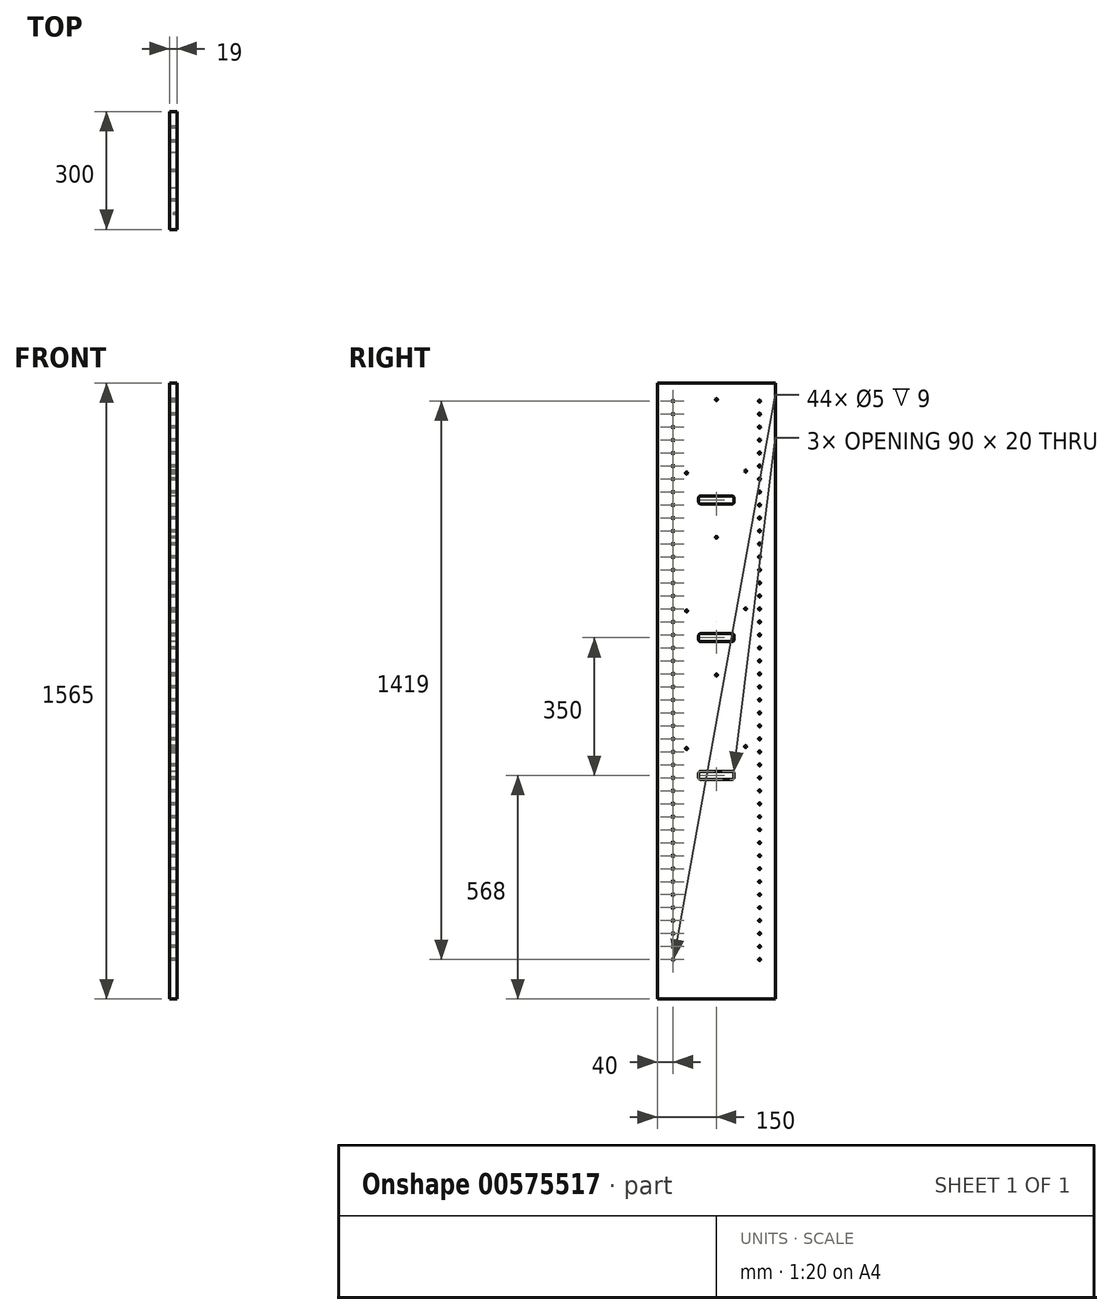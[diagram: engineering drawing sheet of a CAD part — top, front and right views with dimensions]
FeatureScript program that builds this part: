
annotation { "Feature Type Name" : "Feature", "Feature Type Description" : "" }
export const myFeature = defineFeature(function(context is Context, id is Id, definition is map)
    precondition{}
    {
        {
            var Q0;
            Q0=qCreatedBy(makeId("Front.planeOp"),FACE);
            var sketch = newSketch(context, id + "F0", { "sketchPlane" : qUnion([Q0])});
            skLineSegment(sketch, "E0.bottom", {"start": v(0, 0) * mm, "end": v(1000, 0) * mm, "construction": true});
            skLineSegment(sketch, "E0.left", {"start": v(0, 0) * mm, "end": v(0, 1590) * mm, "construction": true});
            skLineSegment(sketch, "E0.right", {"start": v(1000, 0) * mm, "end": v(1000, 1590) * mm, "construction": true});
            skLineSegment(sketch, "E1", {"start": v(500, 1590) * mm, "end": v(500, 0) * mm, "construction": true});
            skLineSegment(sketch, "E2.bottom", {"start": v(0, 1590) * mm, "end": v(1000, 1590) * mm, "construction": true});
            skLineSegment(sketch, "E2.left", {"start": v(0, 1590) * mm, "end": v(0, 290) * mm, "construction": true});
            skSolve(sketch);
        }
        {
            var Q0;
            Q0=qCreatedBy(makeId("Right.planeOp"),FACE);
            var sketch = newSketch(context, id + "F1", { "sketchPlane" : qUnion([Q0])});
            skLineSegment(sketch, "E3.bottom", {"start": v(0, 1590) * mm, "end": v(300, 1590) * mm});
            skLineSegment(sketch, "E3.top", {"start": v(0, 25) * mm, "end": v(300, 25) * mm});
            skLineSegment(sketch, "E3.left", {"start": v(0, 1590) * mm, "end": v(0, 25) * mm});
            skLineSegment(sketch, "E3.right", {"start": v(300, 1590) * mm, "end": v(300, 25) * mm});
            skCircle(sketch, "E4", {"center": v(150, 1548) * mm, "radius": 2.5 * mm});
            skCircle(sketch, "E5", {"center": v(74.47, 1361.2) * mm, "radius": 2.5 * mm});
            skCircle(sketch, "E6.MirrorC", {"center": v(224.47, 1366.34) * mm, "radius": 2.5 * mm});
            skLineSegment(sketch, "E7.bottom", {"start": v(190, 1283) * mm, "end": v(110, 1283) * mm});
            skLineSegment(sketch, "E7.top", {"start": v(190, 1303) * mm, "end": v(110, 1303) * mm});
            skLineSegment(sketch, "E7.left", {"start": v(195, 1288) * mm, "end": v(195, 1298) * mm});
            skLineSegment(sketch, "E7.right", {"start": v(105, 1288) * mm, "end": v(105, 1298) * mm});
            skPoint(sketch, "E7.middle", {"position": v(150, 1293) * mm});
            skPoint(sketch, "E8.visualSharp", {"position": v(105, 1303) * mm});
            skArc(sketch, "E8.filletArc", {"start": v(110, 1303) * mm, "mid": v(106.46, 1301.54) * mm, "end": v(105, 1298) * mm});
            skPoint(sketch, "E9.visualSharp", {"position": v(105, 1283) * mm});
            skArc(sketch, "E9.filletArc", {"start": v(105, 1288) * mm, "mid": v(106.46, 1284.46) * mm, "end": v(110, 1283) * mm});
            skPoint(sketch, "E10.visualSharp", {"position": v(195, 1283) * mm});
            skArc(sketch, "E10.filletArc", {"start": v(190, 1283) * mm, "mid": v(193.54, 1284.46) * mm, "end": v(195, 1288) * mm});
            skPoint(sketch, "E11.visualSharp", {"position": v(195, 1303) * mm});
            skArc(sketch, "E11.filletArc", {"start": v(195, 1298) * mm, "mid": v(193.54, 1301.54) * mm, "end": v(190, 1303) * mm});
            skLineSegment(sketch, "E12", {"start": v(150, 1590) * mm, "end": v(150, 25) * mm, "construction": true});
            skLineSegment(sketch, "E13.0.1.0", {"start": v(190, 933) * mm, "end": v(110, 933) * mm});
            skLineSegment(sketch, "E13.0.1.1", {"start": v(190, 953) * mm, "end": v(110, 953) * mm});
            skPoint(sketch, "E13.0.1.2", {"position": v(195, 933) * mm});
            skPoint(sketch, "E13.0.1.3", {"position": v(150, 943) * mm});
            skPoint(sketch, "E13.0.1.4", {"position": v(195, 953) * mm});
            skPoint(sketch, "E13.0.1.5", {"position": v(105, 933) * mm});
            skCircle(sketch, "E13.0.1.6", {"center": v(150, 1198) * mm, "radius": 2.5 * mm});
            skCircle(sketch, "E13.0.1.7", {"center": v(74.47, 1011.2) * mm, "radius": 2.5 * mm});
            skPoint(sketch, "E13.0.1.8", {"position": v(105, 953) * mm});
            skCircle(sketch, "E13.0.1.9", {"center": v(224.47, 1016.34) * mm, "radius": 2.5 * mm});
            skArc(sketch, "E13.0.1.10", {"start": v(110, 953) * mm, "mid": v(106.46, 951.54) * mm, "end": v(105, 948) * mm});
            skLineSegment(sketch, "E13.0.1.11", {"start": v(105, 938) * mm, "end": v(105, 948) * mm});
            skLineSegment(sketch, "E13.0.1.12", {"start": v(195, 938) * mm, "end": v(195, 948) * mm});
            skArc(sketch, "E13.0.1.13", {"start": v(105, 938) * mm, "mid": v(106.46, 934.46) * mm, "end": v(110, 933) * mm});
            skArc(sketch, "E13.0.1.14", {"start": v(195, 948) * mm, "mid": v(193.54, 951.54) * mm, "end": v(190, 953) * mm});
            skArc(sketch, "E13.0.1.15", {"start": v(190, 933) * mm, "mid": v(193.54, 934.46) * mm, "end": v(195, 938) * mm});
            skLineSegment(sketch, "E13.0.2.0", {"start": v(190, 583) * mm, "end": v(110, 583) * mm});
            skLineSegment(sketch, "E13.0.2.1", {"start": v(190, 603) * mm, "end": v(110, 603) * mm});
            skPoint(sketch, "E13.0.2.2", {"position": v(195, 583) * mm});
            skPoint(sketch, "E13.0.2.3", {"position": v(150, 593) * mm});
            skPoint(sketch, "E13.0.2.4", {"position": v(195, 603) * mm});
            skPoint(sketch, "E13.0.2.5", {"position": v(105, 583) * mm});
            skCircle(sketch, "E13.0.2.6", {"center": v(150, 848) * mm, "radius": 2.5 * mm});
            skCircle(sketch, "E13.0.2.7", {"center": v(74.47, 661.2) * mm, "radius": 2.5 * mm});
            skPoint(sketch, "E13.0.2.8", {"position": v(105, 603) * mm});
            skCircle(sketch, "E13.0.2.9", {"center": v(224.47, 666.34) * mm, "radius": 2.5 * mm});
            skArc(sketch, "E13.0.2.10", {"start": v(110, 603) * mm, "mid": v(106.46, 601.54) * mm, "end": v(105, 598) * mm});
            skLineSegment(sketch, "E13.0.2.11", {"start": v(105, 588) * mm, "end": v(105, 598) * mm});
            skLineSegment(sketch, "E13.0.2.12", {"start": v(195, 588) * mm, "end": v(195, 598) * mm});
            skArc(sketch, "E13.0.2.13", {"start": v(105, 588) * mm, "mid": v(106.46, 584.46) * mm, "end": v(110, 583) * mm});
            skArc(sketch, "E13.0.2.14", {"start": v(195, 598) * mm, "mid": v(193.54, 601.54) * mm, "end": v(190, 603) * mm});
            skArc(sketch, "E13.0.2.15", {"start": v(190, 583) * mm, "mid": v(193.54, 584.46) * mm, "end": v(195, 588) * mm});
            skLineSegment(sketch, "E13.direction1", {"start": v(105, 1283) * mm, "end": v(130, 1283) * mm, "construction": true});
            skLineSegment(sketch, "E13.direction2", {"start": v(105, 1283) * mm, "end": v(105, 933) * mm, "construction": true});
            skCircle(sketch, "E14", {"center": v(40, 125) * mm, "radius": 2.5 * mm});
            skCircle(sketch, "E15.0.1.0", {"center": v(40, 158) * mm, "radius": 2.5 * mm});
            skCircle(sketch, "E15.0.2.0", {"center": v(40, 191) * mm, "radius": 2.5 * mm});
            skCircle(sketch, "E15.0.3.0", {"center": v(40, 224) * mm, "radius": 2.5 * mm});
            skCircle(sketch, "E15.0.4.0", {"center": v(40, 257) * mm, "radius": 2.5 * mm});
            skCircle(sketch, "E15.0.5.0", {"center": v(40, 290) * mm, "radius": 2.5 * mm});
            skCircle(sketch, "E15.0.6.0", {"center": v(40, 323) * mm, "radius": 2.5 * mm});
            skCircle(sketch, "E15.0.7.0", {"center": v(40, 356) * mm, "radius": 2.5 * mm});
            skCircle(sketch, "E15.0.8.0", {"center": v(40, 389) * mm, "radius": 2.5 * mm});
            skCircle(sketch, "E15.0.9.0", {"center": v(40, 422) * mm, "radius": 2.5 * mm});
            skCircle(sketch, "E15.0.10.0", {"center": v(40, 455) * mm, "radius": 2.5 * mm});
            skCircle(sketch, "E15.0.11.0", {"center": v(40, 488) * mm, "radius": 2.5 * mm});
            skCircle(sketch, "E15.0.12.0", {"center": v(40, 521) * mm, "radius": 2.5 * mm});
            skCircle(sketch, "E15.0.13.0", {"center": v(40, 554) * mm, "radius": 2.5 * mm});
            skCircle(sketch, "E15.0.14.0", {"center": v(40, 587) * mm, "radius": 2.5 * mm});
            skCircle(sketch, "E15.0.15.0", {"center": v(40, 620) * mm, "radius": 2.5 * mm});
            skCircle(sketch, "E15.0.16.0", {"center": v(40, 653) * mm, "radius": 2.5 * mm});
            skCircle(sketch, "E15.0.17.0", {"center": v(40, 686) * mm, "radius": 2.5 * mm});
            skCircle(sketch, "E15.0.18.0", {"center": v(40, 719) * mm, "radius": 2.5 * mm});
            skCircle(sketch, "E15.0.19.0", {"center": v(40, 752) * mm, "radius": 2.5 * mm});
            skCircle(sketch, "E15.0.20.0", {"center": v(40, 785) * mm, "radius": 2.5 * mm});
            skCircle(sketch, "E15.0.21.0", {"center": v(40, 818) * mm, "radius": 2.5 * mm});
            skCircle(sketch, "E15.0.22.0", {"center": v(40, 851) * mm, "radius": 2.5 * mm});
            skCircle(sketch, "E15.0.23.0", {"center": v(40, 884) * mm, "radius": 2.5 * mm});
            skCircle(sketch, "E15.0.24.0", {"center": v(40, 917) * mm, "radius": 2.5 * mm});
            skCircle(sketch, "E15.0.25.0", {"center": v(40, 950) * mm, "radius": 2.5 * mm});
            skCircle(sketch, "E15.0.26.0", {"center": v(40, 983) * mm, "radius": 2.5 * mm});
            skCircle(sketch, "E15.0.27.0", {"center": v(40, 1016) * mm, "radius": 2.5 * mm});
            skCircle(sketch, "E15.0.28.0", {"center": v(40, 1049) * mm, "radius": 2.5 * mm});
            skCircle(sketch, "E15.0.29.0", {"center": v(40, 1082) * mm, "radius": 2.5 * mm});
            skCircle(sketch, "E15.0.30.0", {"center": v(40, 1115) * mm, "radius": 2.5 * mm});
            skCircle(sketch, "E15.0.31.0", {"center": v(40, 1148) * mm, "radius": 2.5 * mm});
            skCircle(sketch, "E15.0.32.0", {"center": v(40, 1181) * mm, "radius": 2.5 * mm});
            skCircle(sketch, "E15.0.33.0", {"center": v(40, 1214) * mm, "radius": 2.5 * mm});
            skCircle(sketch, "E15.0.34.0", {"center": v(40, 1247) * mm, "radius": 2.5 * mm});
            skCircle(sketch, "E15.0.35.0", {"center": v(40, 1280) * mm, "radius": 2.5 * mm});
            skCircle(sketch, "E15.0.36.0", {"center": v(40, 1313) * mm, "radius": 2.5 * mm});
            skCircle(sketch, "E15.0.37.0", {"center": v(40, 1346) * mm, "radius": 2.5 * mm});
            skCircle(sketch, "E15.0.38.0", {"center": v(40, 1379) * mm, "radius": 2.5 * mm});
            skCircle(sketch, "E15.0.39.0", {"center": v(40, 1412) * mm, "radius": 2.5 * mm});
            skLineSegment(sketch, "E15.direction1", {"start": v(40, 125) * mm, "end": v(65, 125) * mm, "construction": true});
            skLineSegment(sketch, "E15.direction2", {"start": v(40, 125) * mm, "end": v(40, 158) * mm, "construction": true});
            skCircle(sketch, "E16.MirrorC", {"center": v(260, 125) * mm, "radius": 2.5 * mm});
            skCircle(sketch, "E17.MirrorC", {"center": v(260, 158) * mm, "radius": 2.5 * mm});
            skCircle(sketch, "E18.MirrorC", {"center": v(260, 191) * mm, "radius": 2.5 * mm});
            skCircle(sketch, "E19.0.0.40", {"center": v(40, 1445) * mm, "radius": 2.5 * mm});
            skCircle(sketch, "E19.0.0.41", {"center": v(40, 1478) * mm, "radius": 2.5 * mm});
            skCircle(sketch, "E19.0.0.42", {"center": v(40, 1511) * mm, "radius": 2.5 * mm});
            skCircle(sketch, "E19.0.0.43", {"center": v(40, 1544) * mm, "radius": 2.5 * mm});
            skCircle(sketch, "E20.MirrorC", {"center": v(260, 1478) * mm, "radius": 2.5 * mm});
            skCircle(sketch, "E21.MirrorC", {"center": v(260, 1280) * mm, "radius": 2.5 * mm});
            skCircle(sketch, "E22.MirrorC", {"center": v(260, 1313) * mm, "radius": 2.5 * mm});
            skCircle(sketch, "E23.MirrorC", {"center": v(260, 1082) * mm, "radius": 2.5 * mm});
            skCircle(sketch, "E24.MirrorC", {"center": v(260, 1049) * mm, "radius": 2.5 * mm});
            skCircle(sketch, "E25.MirrorC", {"center": v(260, 1346) * mm, "radius": 2.5 * mm});
            skCircle(sketch, "E26.MirrorC", {"center": v(260, 1445) * mm, "radius": 2.5 * mm});
            skCircle(sketch, "E27.MirrorC", {"center": v(260, 1412) * mm, "radius": 2.5 * mm});
            skCircle(sketch, "E28.MirrorC", {"center": v(260, 1214) * mm, "radius": 2.5 * mm});
            skCircle(sketch, "E29.MirrorC", {"center": v(260, 1247) * mm, "radius": 2.5 * mm});
            skCircle(sketch, "E30.MirrorC", {"center": v(260, 1181) * mm, "radius": 2.5 * mm});
            skCircle(sketch, "E31.MirrorC", {"center": v(260, 1148) * mm, "radius": 2.5 * mm});
            skCircle(sketch, "E32.MirrorC", {"center": v(260, 1511) * mm, "radius": 2.5 * mm});
            skCircle(sketch, "E33.MirrorC", {"center": v(260, 1544) * mm, "radius": 2.5 * mm});
            skCircle(sketch, "E34.MirrorC", {"center": v(260, 1016) * mm, "radius": 2.5 * mm});
            skCircle(sketch, "E35.MirrorC", {"center": v(260, 1115) * mm, "radius": 2.5 * mm});
            skCircle(sketch, "E36.MirrorC", {"center": v(260, 1379) * mm, "radius": 2.5 * mm});
            skCircle(sketch, "E37.MirrorC", {"center": v(260, 752) * mm, "radius": 2.5 * mm});
            skCircle(sketch, "E38.MirrorC", {"center": v(260, 653) * mm, "radius": 2.5 * mm});
            skCircle(sketch, "E39.MirrorC", {"center": v(260, 554) * mm, "radius": 2.5 * mm});
            skCircle(sketch, "E40.MirrorC", {"center": v(260, 521) * mm, "radius": 2.5 * mm});
            skCircle(sketch, "E41.MirrorC", {"center": v(260, 917) * mm, "radius": 2.5 * mm});
            skCircle(sketch, "E42.MirrorC", {"center": v(260, 785) * mm, "radius": 2.5 * mm});
            skCircle(sketch, "E43.MirrorC", {"center": v(260, 719) * mm, "radius": 2.5 * mm});
            skCircle(sketch, "E44.MirrorC", {"center": v(260, 587) * mm, "radius": 2.5 * mm});
            skCircle(sketch, "E45.MirrorC", {"center": v(260, 950) * mm, "radius": 2.5 * mm});
            skCircle(sketch, "E46.MirrorC", {"center": v(260, 455) * mm, "radius": 2.5 * mm});
            skCircle(sketch, "E47.MirrorC", {"center": v(260, 983) * mm, "radius": 2.5 * mm});
            skCircle(sketch, "E48.MirrorC", {"center": v(260, 488) * mm, "radius": 2.5 * mm});
            skCircle(sketch, "E49.MirrorC", {"center": v(260, 851) * mm, "radius": 2.5 * mm});
            skCircle(sketch, "E50.MirrorC", {"center": v(260, 818) * mm, "radius": 2.5 * mm});
            skCircle(sketch, "E51.MirrorC", {"center": v(260, 884) * mm, "radius": 2.5 * mm});
            skCircle(sketch, "E52.MirrorC", {"center": v(260, 686) * mm, "radius": 2.5 * mm});
            skCircle(sketch, "E53.MirrorC", {"center": v(260, 620) * mm, "radius": 2.5 * mm});
            skCircle(sketch, "E54.MirrorC", {"center": v(260, 290) * mm, "radius": 2.5 * mm});
            skCircle(sketch, "E55.MirrorC", {"center": v(260, 422) * mm, "radius": 2.5 * mm});
            skCircle(sketch, "E56.MirrorC", {"center": v(260, 224) * mm, "radius": 2.5 * mm});
            skCircle(sketch, "E57.MirrorC", {"center": v(260, 257) * mm, "radius": 2.5 * mm});
            skCircle(sketch, "E58.MirrorC", {"center": v(260, 323) * mm, "radius": 2.5 * mm});
            skCircle(sketch, "E59.MirrorC", {"center": v(260, 389) * mm, "radius": 2.5 * mm});
            skCircle(sketch, "E60.MirrorC", {"center": v(260, 356) * mm, "radius": 2.5 * mm});
            skSolve(sketch);
        }
        {
            var Q0;
            Q0=makeQuery(id+"F1.imprint","IMPRINT",FACE,{"disambiguationData":[TD([[makeQuery(id+"F1.imprint","IMPRINT",EDGE,{"derivedFrom":sQuery(id+"F1.wireOp",EDGE,"E35.MirrorC")}),-1.0]])]});
            var Q1;
            Q1=makeQuery(id+"F1.imprint","IMPRINT",FACE,{"disambiguationData":[TD([[makeQuery(id+"F1.imprint","IMPRINT",EDGE,{"derivedFrom":sQuery(id+"F1.wireOp",EDGE,"E51.MirrorC")}),-1.0]])]});
            var Q2;
            Q2=makeQuery(id+"F1.imprint","IMPRINT",FACE,{"disambiguationData":[TD([[makeQuery(id+"F1.imprint","IMPRINT",EDGE,{"derivedFrom":sQuery(id+"F1.wireOp",EDGE,"E52.MirrorC")}),-1.0]])]});
            var Q3;
            Q3=makeQuery(id+"F1.imprint","IMPRINT",FACE,{"disambiguationData":[TD([[makeQuery(id+"F1.imprint","IMPRINT",EDGE,{"derivedFrom":sQuery(id+"F1.wireOp",EDGE,"E33.MirrorC")}),-1.0]])]});
            var Q4;
            Q4=makeQuery(id+"F1.imprint","IMPRINT",FACE,{"disambiguationData":[TD([[makeQuery(id+"F1.imprint","IMPRINT",EDGE,{"derivedFrom":sQuery(id+"F1.wireOp",EDGE,"E28.MirrorC")}),-1.0]])]});
            var Q5;
            Q5=makeQuery(id+"F1.imprint","IMPRINT",FACE,{"disambiguationData":[TD([[makeQuery(id+"F1.imprint","IMPRINT",EDGE,{"derivedFrom":sQuery(id+"F1.wireOp",EDGE,"E41.MirrorC")}),-1.0]])]});
            var Q6;
            Q6=makeQuery(id+"F1.imprint","IMPRINT",FACE,{"disambiguationData":[TD([[makeQuery(id+"F1.imprint","IMPRINT",EDGE,{"derivedFrom":sQuery(id+"F1.wireOp",EDGE,"E42.MirrorC")}),-1.0]])]});
            var Q7;
            Q7=makeQuery(id+"F1.imprint","IMPRINT",FACE,{"disambiguationData":[TD([[makeQuery(id+"F1.imprint","IMPRINT",EDGE,{"derivedFrom":sQuery(id+"F1.wireOp",EDGE,"E26.MirrorC")}),-1.0]])]});
            var Q8;
            Q8=makeQuery(id+"F1.imprint","IMPRINT",FACE,{"disambiguationData":[TD([[makeQuery(id+"F1.imprint","IMPRINT",EDGE,{"derivedFrom":sQuery(id+"F1.wireOp",EDGE,"E37.MirrorC")}),-1.0]])]});
            var Q9;
            Q9=makeQuery(id+"F1.imprint","IMPRINT",FACE,{"disambiguationData":[TD([[makeQuery(id+"F1.imprint","IMPRINT",EDGE,{"derivedFrom":sQuery(id+"F1.wireOp",EDGE,"E43.MirrorC")}),-1.0]])]});
            var Q10;
            Q10=makeQuery(id+"F1.imprint","IMPRINT",FACE,{"disambiguationData":[TD([[makeQuery(id+"F1.imprint","IMPRINT",EDGE,{"derivedFrom":sQuery(id+"F1.wireOp",EDGE,"E53.MirrorC")}),-1.0]])]});
            var Q11;
            Q11=makeQuery(id+"F1.imprint","IMPRINT",FACE,{"disambiguationData":[TD([[makeQuery(id+"F1.imprint","IMPRINT",EDGE,{"derivedFrom":sQuery(id+"F1.wireOp",EDGE,"E25.MirrorC")}),-1.0]])]});
            var Q12;
            Q12=makeQuery(id+"F1.imprint","IMPRINT",FACE,{"disambiguationData":[TD([[makeQuery(id+"F1.imprint","IMPRINT",EDGE,{"derivedFrom":sQuery(id+"F1.wireOp",EDGE,"E29.MirrorC")}),-1.0]])]});
            var Q13;
            Q13=makeQuery(id+"F1.imprint","IMPRINT",FACE,{"disambiguationData":[TD([[makeQuery(id+"F1.imprint","IMPRINT",EDGE,{"derivedFrom":sQuery(id+"F1.wireOp",EDGE,"E45.MirrorC")}),-1.0]])]});
            var Q14;
            Q14=makeQuery(id+"F1.imprint","IMPRINT",FACE,{"disambiguationData":[TD([[makeQuery(id+"F1.imprint","IMPRINT",EDGE,{"derivedFrom":sQuery(id+"F1.wireOp",EDGE,"E30.MirrorC")}),-1.0]])]});
            var Q15;
            Q15=makeQuery(id+"F1.imprint","IMPRINT",FACE,{"disambiguationData":[TD([[makeQuery(id+"F1.imprint","IMPRINT",EDGE,{"derivedFrom":sQuery(id+"F1.wireOp",EDGE,"E50.MirrorC")}),-1.0]])]});
            var Q16;
            Q16=makeQuery(id+"F1.imprint","IMPRINT",FACE,{"disambiguationData":[TD([[makeQuery(id+"F1.imprint","IMPRINT",EDGE,{"derivedFrom":sQuery(id+"F1.wireOp",EDGE,"E44.MirrorC")}),-1.0]])]});
            var Q17;
            Q17=makeQuery(id+"F1.imprint","IMPRINT",FACE,{"disambiguationData":[TD([[makeQuery(id+"F1.imprint","IMPRINT",EDGE,{"derivedFrom":sQuery(id+"F1.wireOp",EDGE,"E38.MirrorC")}),-1.0]])]});
            var Q18;
            Q18=makeQuery(id+"F1.imprint","IMPRINT",FACE,{"disambiguationData":[TD([[makeQuery(id+"F1.imprint","IMPRINT",EDGE,{"derivedFrom":sQuery(id+"F1.wireOp",EDGE,"E34.MirrorC")}),-1.0]])]});
            var Q19;
            Q19=makeQuery(id+"F1.imprint","IMPRINT",FACE,{"disambiguationData":[TD([[makeQuery(id+"F1.imprint","IMPRINT",EDGE,{"derivedFrom":sQuery(id+"F1.wireOp",EDGE,"E24.MirrorC")}),-1.0]])]});
            var Q20;
            Q20=makeQuery(id+"F1.imprint","IMPRINT",FACE,{"disambiguationData":[TD([[makeQuery(id+"F1.imprint","IMPRINT",EDGE,{"derivedFrom":sQuery(id+"F1.wireOp",EDGE,"E31.MirrorC")}),-1.0]])]});
            var Q21;
            Q21=makeQuery(id+"F1.imprint","IMPRINT",FACE,{"disambiguationData":[TD([[makeQuery(id+"F1.imprint","IMPRINT",EDGE,{"derivedFrom":sQuery(id+"F1.wireOp",EDGE,"E32.MirrorC")}),-1.0]])]});
            var Q22;
            Q22=makeQuery(id+"F1.imprint","IMPRINT",FACE,{"disambiguationData":[TD([[makeQuery(id+"F1.imprint","IMPRINT",EDGE,{"derivedFrom":sQuery(id+"F1.wireOp",EDGE,"E27.MirrorC")}),-1.0]])]});
            var Q23;
            Q23=makeQuery(id+"F1.imprint","IMPRINT",FACE,{"disambiguationData":[TD([[makeQuery(id+"F1.imprint","IMPRINT",EDGE,{"derivedFrom":sQuery(id+"F1.wireOp",EDGE,"E47.MirrorC")}),-1.0]])]});
            var Q24;
            Q24=makeQuery(id+"F1.imprint","IMPRINT",FACE,{"disambiguationData":[TD([[makeQuery(id+"F1.imprint","IMPRINT",EDGE,{"derivedFrom":sQuery(id+"F1.wireOp",EDGE,"E22.MirrorC")}),-1.0]])]});
            var Q25;
            Q25=makeQuery(id+"F1.imprint","IMPRINT",FACE,{"disambiguationData":[TD([[makeQuery(id+"F1.imprint","IMPRINT",EDGE,{"derivedFrom":sQuery(id+"F1.wireOp",EDGE,"E20.MirrorC")}),-1.0]])]});
            var Q26;
            Q26=makeQuery(id+"F1.imprint","IMPRINT",FACE,{"disambiguationData":[TD([[makeQuery(id+"F1.imprint","IMPRINT",EDGE,{"derivedFrom":sQuery(id+"F1.wireOp",EDGE,"E49.MirrorC")}),-1.0]])]});
            var Q27;
            Q27=makeQuery(id+"F1.imprint","IMPRINT",FACE,{"disambiguationData":[TD([[makeQuery(id+"F1.imprint","IMPRINT",EDGE,{"derivedFrom":sQuery(id+"F1.wireOp",EDGE,"E36.MirrorC")}),-1.0]])]});
            var Q28;
            Q28=makeQuery(id+"F1.imprint","IMPRINT",FACE,{"disambiguationData":[TD([[makeQuery(id+"F1.imprint","IMPRINT",EDGE,{"derivedFrom":sQuery(id+"F1.wireOp",EDGE,"E23.MirrorC")}),-1.0]])]});
            var Q29;
            Q29=makeQuery(id+"F1.imprint","IMPRINT",FACE,{"disambiguationData":[TD([[makeQuery(id+"F1.imprint","IMPRINT",EDGE,{"derivedFrom":sQuery(id+"F1.wireOp",EDGE,"E21.MirrorC")}),-1.0]])]});
            var Q30;
            Q30=makeQuery(id+"F1.imprint","IMPRINT",FACE,{"disambiguationData":[TD([[makeQuery(id+"F1.imprint","IMPRINT",EDGE,{"derivedFrom":sQuery(id+"F1.wireOp",EDGE,"E15.0.14.0")}),1.0]])]});
            var Q31;
            Q31=makeQuery(id+"F1.imprint","IMPRINT",FACE,{"disambiguationData":[TD([[makeQuery(id+"F1.imprint","IMPRINT",EDGE,{"derivedFrom":sQuery(id+"F1.wireOp",EDGE,"E15.0.16.0")}),1.0]])]});
            var Q32;
            Q32=makeQuery(id+"F1.imprint","IMPRINT",FACE,{"disambiguationData":[TD([[makeQuery(id+"F1.imprint","IMPRINT",EDGE,{"derivedFrom":sQuery(id+"F1.wireOp",EDGE,"E15.0.15.0")}),1.0]])]});
            var Q33;
            Q33=makeQuery(id+"F1.imprint","IMPRINT",FACE,{"disambiguationData":[TD([[makeQuery(id+"F1.imprint","IMPRINT",EDGE,{"derivedFrom":sQuery(id+"F1.wireOp",EDGE,"E15.0.9.0")}),1.0]])]});
            var Q34;
            Q34=makeQuery(id+"F1.imprint","IMPRINT",FACE,{"disambiguationData":[TD([[makeQuery(id+"F1.imprint","IMPRINT",EDGE,{"derivedFrom":sQuery(id+"F1.wireOp",EDGE,"E19.0.0.41")}),1.0]])]});
            var Q35;
            Q35=makeQuery(id+"F1.imprint","IMPRINT",FACE,{"disambiguationData":[TD([[makeQuery(id+"F1.imprint","IMPRINT",EDGE,{"derivedFrom":sQuery(id+"F1.wireOp",EDGE,"E15.0.8.0")}),1.0]])]});
            var Q36;
            Q36=makeQuery(id+"F1.imprint","IMPRINT",FACE,{"disambiguationData":[TD([[makeQuery(id+"F1.imprint","IMPRINT",EDGE,{"derivedFrom":sQuery(id+"F1.wireOp",EDGE,"E15.0.26.0")}),1.0]])]});
            var Q37;
            Q37=makeQuery(id+"F1.imprint","IMPRINT",FACE,{"disambiguationData":[TD([[makeQuery(id+"F1.imprint","IMPRINT",EDGE,{"derivedFrom":sQuery(id+"F1.wireOp",EDGE,"E15.0.37.0")}),1.0]])]});
            var Q38;
            Q38=makeQuery(id+"F1.imprint","IMPRINT",FACE,{"disambiguationData":[TD([[makeQuery(id+"F1.imprint","IMPRINT",EDGE,{"derivedFrom":sQuery(id+"F1.wireOp",EDGE,"E15.0.21.0")}),1.0]])]});
            var Q39;
            Q39=makeQuery(id+"F1.imprint","IMPRINT",FACE,{"disambiguationData":[TD([[makeQuery(id+"F1.imprint","IMPRINT",EDGE,{"derivedFrom":sQuery(id+"F1.wireOp",EDGE,"E15.0.22.0")}),1.0]])]});
            var Q40;
            Q40=makeQuery(id+"F1.imprint","IMPRINT",FACE,{"disambiguationData":[TD([[makeQuery(id+"F1.imprint","IMPRINT",EDGE,{"derivedFrom":sQuery(id+"F1.wireOp",EDGE,"E15.0.10.0")}),1.0]])]});
            var Q41;
            Q41=makeQuery(id+"F1.imprint","IMPRINT",FACE,{"disambiguationData":[TD([[makeQuery(id+"F1.imprint","IMPRINT",EDGE,{"derivedFrom":sQuery(id+"F1.wireOp",EDGE,"E15.0.18.0")}),1.0]])]});
            var Q42;
            Q42=makeQuery(id+"F1.imprint","IMPRINT",FACE,{"disambiguationData":[TD([[makeQuery(id+"F1.imprint","IMPRINT",EDGE,{"derivedFrom":sQuery(id+"F1.wireOp",EDGE,"E15.0.7.0")}),1.0]])]});
            var Q43;
            Q43=makeQuery(id+"F1.imprint","IMPRINT",FACE,{"disambiguationData":[TD([[makeQuery(id+"F1.imprint","IMPRINT",EDGE,{"derivedFrom":sQuery(id+"F1.wireOp",EDGE,"E15.0.4.0")}),1.0]])]});
            var Q44;
            Q44=makeQuery(id+"F1.imprint","IMPRINT",FACE,{"disambiguationData":[TD([[makeQuery(id+"F1.imprint","IMPRINT",EDGE,{"derivedFrom":sQuery(id+"F1.wireOp",EDGE,"E15.0.20.0")}),1.0]])]});
            var Q45;
            Q45=makeQuery(id+"F1.imprint","IMPRINT",FACE,{"disambiguationData":[TD([[makeQuery(id+"F1.imprint","IMPRINT",EDGE,{"derivedFrom":sQuery(id+"F1.wireOp",EDGE,"E15.0.29.0")}),1.0]])]});
            var Q46;
            Q46=makeQuery(id+"F1.imprint","IMPRINT",FACE,{"disambiguationData":[TD([[makeQuery(id+"F1.imprint","IMPRINT",EDGE,{"derivedFrom":sQuery(id+"F1.wireOp",EDGE,"E19.0.0.42")}),1.0]])]});
            var Q47;
            Q47=makeQuery(id+"F1.imprint","IMPRINT",FACE,{"disambiguationData":[TD([[makeQuery(id+"F1.imprint","IMPRINT",EDGE,{"derivedFrom":sQuery(id+"F1.wireOp",EDGE,"E15.0.28.0")}),1.0]])]});
            var Q48;
            Q48=makeQuery(id+"F1.imprint","IMPRINT",FACE,{"disambiguationData":[TD([[makeQuery(id+"F1.imprint","IMPRINT",EDGE,{"derivedFrom":sQuery(id+"F1.wireOp",EDGE,"E15.0.13.0")}),1.0]])]});
            var Q49;
            Q49=makeQuery(id+"F1.imprint","IMPRINT",FACE,{"disambiguationData":[TD([[makeQuery(id+"F1.imprint","IMPRINT",EDGE,{"derivedFrom":sQuery(id+"F1.wireOp",EDGE,"E15.0.23.0")}),1.0]])]});
            var Q50;
            Q50=makeQuery(id+"F1.imprint","IMPRINT",FACE,{"disambiguationData":[TD([[makeQuery(id+"F1.imprint","IMPRINT",EDGE,{"derivedFrom":sQuery(id+"F1.wireOp",EDGE,"E15.0.36.0")}),1.0]])]});
            var Q51;
            Q51=makeQuery(id+"F1.imprint","IMPRINT",FACE,{"disambiguationData":[TD([[makeQuery(id+"F1.imprint","IMPRINT",EDGE,{"derivedFrom":sQuery(id+"F1.wireOp",EDGE,"E15.0.32.0")}),1.0]])]});
            var Q52;
            Q52=makeQuery(id+"F1.imprint","IMPRINT",FACE,{"disambiguationData":[TD([[makeQuery(id+"F1.imprint","IMPRINT",EDGE,{"derivedFrom":sQuery(id+"F1.wireOp",EDGE,"E15.0.17.0")}),1.0]])]});
            var Q53;
            Q53=makeQuery(id+"F1.imprint","IMPRINT",FACE,{"disambiguationData":[TD([[makeQuery(id+"F1.imprint","IMPRINT",EDGE,{"derivedFrom":sQuery(id+"F1.wireOp",EDGE,"E19.0.0.43")}),1.0]])]});
            var Q54;
            Q54=makeQuery(id+"F1.imprint","IMPRINT",FACE,{"disambiguationData":[TD([[makeQuery(id+"F1.imprint","IMPRINT",EDGE,{"derivedFrom":sQuery(id+"F1.wireOp",EDGE,"E15.0.31.0")}),1.0]])]});
            var Q55;
            Q55=makeQuery(id+"F1.imprint","IMPRINT",FACE,{"disambiguationData":[TD([[makeQuery(id+"F1.imprint","IMPRINT",EDGE,{"derivedFrom":sQuery(id+"F1.wireOp",EDGE,"E15.0.39.0")}),1.0]])]});
            var Q56;
            Q56=makeQuery(id+"F1.imprint","IMPRINT",FACE,{"disambiguationData":[TD([[makeQuery(id+"F1.imprint","IMPRINT",EDGE,{"derivedFrom":sQuery(id+"F1.wireOp",EDGE,"E15.0.3.0")}),1.0]])]});
            var Q57;
            Q57=makeQuery(id+"F1.imprint","IMPRINT",FACE,{"disambiguationData":[TD([[makeQuery(id+"F1.imprint","IMPRINT",EDGE,{"derivedFrom":sQuery(id+"F1.wireOp",EDGE,"E19.0.0.40")}),1.0]])]});
            var Q58;
            Q58=makeQuery(id+"F1.imprint","IMPRINT",FACE,{"disambiguationData":[TD([[makeQuery(id+"F1.imprint","IMPRINT",EDGE,{"derivedFrom":sQuery(id+"F1.wireOp",EDGE,"E15.0.24.0")}),1.0]])]});
            var Q59;
            Q59=makeQuery(id+"F1.imprint","IMPRINT",FACE,{"disambiguationData":[TD([[makeQuery(id+"F1.imprint","IMPRINT",EDGE,{"derivedFrom":sQuery(id+"F1.wireOp",EDGE,"E15.0.27.0")}),1.0]])]});
            var Q60;
            Q60=makeQuery(id+"F1.imprint","IMPRINT",FACE,{"disambiguationData":[TD([[makeQuery(id+"F1.imprint","IMPRINT",EDGE,{"derivedFrom":sQuery(id+"F1.wireOp",EDGE,"E15.0.25.0")}),1.0]])]});
            var Q61;
            Q61=makeQuery(id+"F1.imprint","IMPRINT",FACE,{"disambiguationData":[TD([[makeQuery(id+"F1.imprint","IMPRINT",EDGE,{"derivedFrom":sQuery(id+"F1.wireOp",EDGE,"E15.0.35.0")}),1.0]])]});
            var Q62;
            Q62=makeQuery(id+"F1.imprint","IMPRINT",FACE,{"disambiguationData":[TD([[makeQuery(id+"F1.imprint","IMPRINT",EDGE,{"derivedFrom":sQuery(id+"F1.wireOp",EDGE,"E15.0.33.0")}),1.0]])]});
            var Q63;
            Q63=makeQuery(id+"F1.imprint","IMPRINT",FACE,{"disambiguationData":[TD([[makeQuery(id+"F1.imprint","IMPRINT",EDGE,{"derivedFrom":sQuery(id+"F1.wireOp",EDGE,"E15.0.19.0")}),1.0]])]});
            var Q64;
            Q64=makeQuery(id+"F1.imprint","IMPRINT",FACE,{"disambiguationData":[TD([[makeQuery(id+"F1.imprint","IMPRINT",EDGE,{"derivedFrom":sQuery(id+"F1.wireOp",EDGE,"E15.0.6.0")}),1.0]])]});
            var Q65;
            Q65=makeQuery(id+"F1.imprint","IMPRINT",FACE,{"disambiguationData":[TD([[makeQuery(id+"F1.imprint","IMPRINT",EDGE,{"derivedFrom":sQuery(id+"F1.wireOp",EDGE,"E15.0.11.0")}),1.0]])]});
            var Q66;
            Q66=makeQuery(id+"F1.imprint","IMPRINT",FACE,{"disambiguationData":[TD([[makeQuery(id+"F1.imprint","IMPRINT",EDGE,{"derivedFrom":sQuery(id+"F1.wireOp",EDGE,"E15.0.34.0")}),1.0]])]});
            var Q67;
            Q67=makeQuery(id+"F1.imprint","IMPRINT",FACE,{"disambiguationData":[TD([[makeQuery(id+"F1.imprint","IMPRINT",EDGE,{"derivedFrom":sQuery(id+"F1.wireOp",EDGE,"E15.0.30.0")}),1.0]])]});
            var Q68;
            Q68=makeQuery(id+"F1.imprint","IMPRINT",FACE,{"disambiguationData":[TD([[makeQuery(id+"F1.imprint","IMPRINT",EDGE,{"derivedFrom":sQuery(id+"F1.wireOp",EDGE,"E15.0.12.0")}),1.0]])]});
            var Q69;
            Q69=makeQuery(id+"F1.imprint","IMPRINT",FACE,{"disambiguationData":[TD([[makeQuery(id+"F1.imprint","IMPRINT",EDGE,{"derivedFrom":sQuery(id+"F1.wireOp",EDGE,"E15.0.5.0")}),1.0]])]});
            var Q70;
            Q70=makeQuery(id+"F1.imprint","IMPRINT",FACE,{"disambiguationData":[TD([[makeQuery(id+"F1.imprint","IMPRINT",EDGE,{"derivedFrom":sQuery(id+"F1.wireOp",EDGE,"E15.0.38.0")}),1.0]])]});
            var Q71;
            Q71=makeQuery(id+"F1.imprint","IMPRINT",FACE,{"disambiguationData":[TD([[makeQuery(id+"F1.imprint","IMPRINT",EDGE,{"derivedFrom":sQuery(id+"F1.wireOp",EDGE,"E40.MirrorC")}),-1.0]])]});
            var Q72;
            Q72=makeQuery(id+"F1.imprint","IMPRINT",FACE,{"disambiguationData":[TD([[makeQuery(id+"F1.imprint","IMPRINT",EDGE,{"derivedFrom":sQuery(id+"F1.wireOp",EDGE,"E59.MirrorC")}),-1.0]])]});
            var Q73;
            Q73=makeQuery(id+"F1.imprint","IMPRINT",FACE,{"disambiguationData":[TD([[makeQuery(id+"F1.imprint","IMPRINT",EDGE,{"derivedFrom":sQuery(id+"F1.wireOp",EDGE,"E18.MirrorC")}),-1.0]])]});
            var Q74;
            Q74=makeQuery(id+"F1.imprint","IMPRINT",FACE,{"disambiguationData":[TD([[makeQuery(id+"F1.imprint","IMPRINT",EDGE,{"derivedFrom":sQuery(id+"F1.wireOp",EDGE,"E55.MirrorC")}),-1.0]])]});
            var Q75;
            Q75=makeQuery(id+"F1.imprint","IMPRINT",FACE,{"disambiguationData":[TD([[makeQuery(id+"F1.imprint","IMPRINT",EDGE,{"derivedFrom":sQuery(id+"F1.wireOp",EDGE,"E16.MirrorC")}),-1.0]])]});
            var Q76;
            Q76=makeQuery(id+"F1.imprint","IMPRINT",FACE,{"disambiguationData":[TD([[makeQuery(id+"F1.imprint","IMPRINT",EDGE,{"derivedFrom":sQuery(id+"F1.wireOp",EDGE,"E56.MirrorC")}),-1.0]])]});
            var Q77;
            Q77=makeQuery(id+"F1.imprint","IMPRINT",FACE,{"disambiguationData":[TD([[makeQuery(id+"F1.imprint","IMPRINT",EDGE,{"derivedFrom":sQuery(id+"F1.wireOp",EDGE,"E54.MirrorC")}),-1.0]])]});
            var Q78;
            Q78=makeQuery(id+"F1.imprint","IMPRINT",FACE,{"disambiguationData":[TD([[makeQuery(id+"F1.imprint","IMPRINT",EDGE,{"derivedFrom":sQuery(id+"F1.wireOp",EDGE,"E46.MirrorC")}),-1.0]])]});
            var Q79;
            Q79=makeQuery(id+"F1.imprint","IMPRINT",FACE,{"disambiguationData":[TD([[makeQuery(id+"F1.imprint","IMPRINT",EDGE,{"derivedFrom":sQuery(id+"F1.wireOp",EDGE,"E48.MirrorC")}),-1.0]])]});
            var Q80;
            Q80=makeQuery(id+"F1.imprint","IMPRINT",FACE,{"disambiguationData":[TD([[makeQuery(id+"F1.imprint","IMPRINT",EDGE,{"derivedFrom":sQuery(id+"F1.wireOp",EDGE,"E57.MirrorC")}),-1.0]])]});
            var Q81;
            Q81=makeQuery(id+"F1.imprint","IMPRINT",FACE,{"disambiguationData":[TD([[makeQuery(id+"F1.imprint","IMPRINT",EDGE,{"derivedFrom":sQuery(id+"F1.wireOp",EDGE,"E17.MirrorC")}),-1.0]])]});
            var Q82;
            Q82=makeQuery(id+"F1.imprint","IMPRINT",FACE,{"disambiguationData":[TD([[makeQuery(id+"F1.imprint","IMPRINT",EDGE,{"derivedFrom":sQuery(id+"F1.wireOp",EDGE,"E60.MirrorC")}),-1.0]])]});
            var Q83;
            Q83=makeQuery(id+"F1.imprint","IMPRINT",FACE,{"disambiguationData":[TD([[makeQuery(id+"F1.imprint","IMPRINT",EDGE,{"derivedFrom":sQuery(id+"F1.wireOp",EDGE,"E39.MirrorC")}),-1.0]])]});
            var Q84;
            Q84=makeQuery(id+"F1.imprint","IMPRINT",FACE,{"disambiguationData":[TD([[makeQuery(id+"F1.imprint","IMPRINT",EDGE,{"derivedFrom":sQuery(id+"F1.wireOp",EDGE,"E58.MirrorC")}),-1.0]])]});
            var Q85;
            Q85=makeQuery(id+"F1.imprint","IMPRINT",FACE,{"disambiguationData":[TD([[makeQuery(id+"F1.imprint","IMPRINT",EDGE,{"derivedFrom":sQuery(id+"F1.wireOp",EDGE,"E15.0.2.0")}),1.0]])]});
            var Q86;
            Q86=makeQuery(id+"F1.imprint","IMPRINT",FACE,{"disambiguationData":[TD([[makeQuery(id+"F1.imprint","IMPRINT",EDGE,{"derivedFrom":sQuery(id+"F1.wireOp",EDGE,"E15.0.1.0")}),1.0]])]});
            var Q87;
            Q87=makeQuery(id+"F1.imprint","IMPRINT",FACE,{"disambiguationData":[TD([[makeQuery(id+"F1.imprint","IMPRINT",EDGE,{"derivedFrom":sQuery(id+"F1.wireOp",EDGE,"E14")}),1.0]])]});
            extrude(context, id + "F2", {"entities" : qUnion([Q0, Q1, Q2, Q3, Q4, Q5, Q6, Q7, Q8, Q9, Q10, Q11, Q12, Q13, Q14, Q15, Q16, Q17, Q18, Q19, Q20, Q21, Q22, Q23, Q24, Q25, Q26, Q27, Q28, Q29, Q30, Q31, Q32, Q33, Q34, Q35, Q36, Q37, Q38, Q39, Q40, Q41, Q42, Q43, Q44, Q45, Q46, Q47, Q48, Q49, Q50, Q51, Q52, Q53, Q54, Q55, Q56, Q57, Q58, Q59, Q60, Q61, Q62, Q63, Q64, Q65, Q66, Q67, Q68, Q69, Q70, Q71, Q72, Q73, Q74, Q75, Q76, Q77, Q78, Q79, Q80, Q81, Q82, Q83, Q84, Q85, Q86, Q87]), "depth" : 10 * mm, "offsetDistance" : 25 * mm});
        }
        {
            var Q0;
            Q0=makeQuery(id+"F1.imprint","IMPRINT",FACE,{"disambiguationData":[TD([[makeQuery(id+"F1.imprint","IMPRINT",EDGE,{"derivedFrom":sQuery(id+"F1.wireOp",EDGE,"E3.bottom")}),-1.0]])]});
            extrude(context, id + "F3", {"entities" : qUnion([Q0]), "operationType" : NewBodyOperationType.ADD, "depth" : 19 * mm, "offsetDistance" : 25 * mm});
        }
    });
